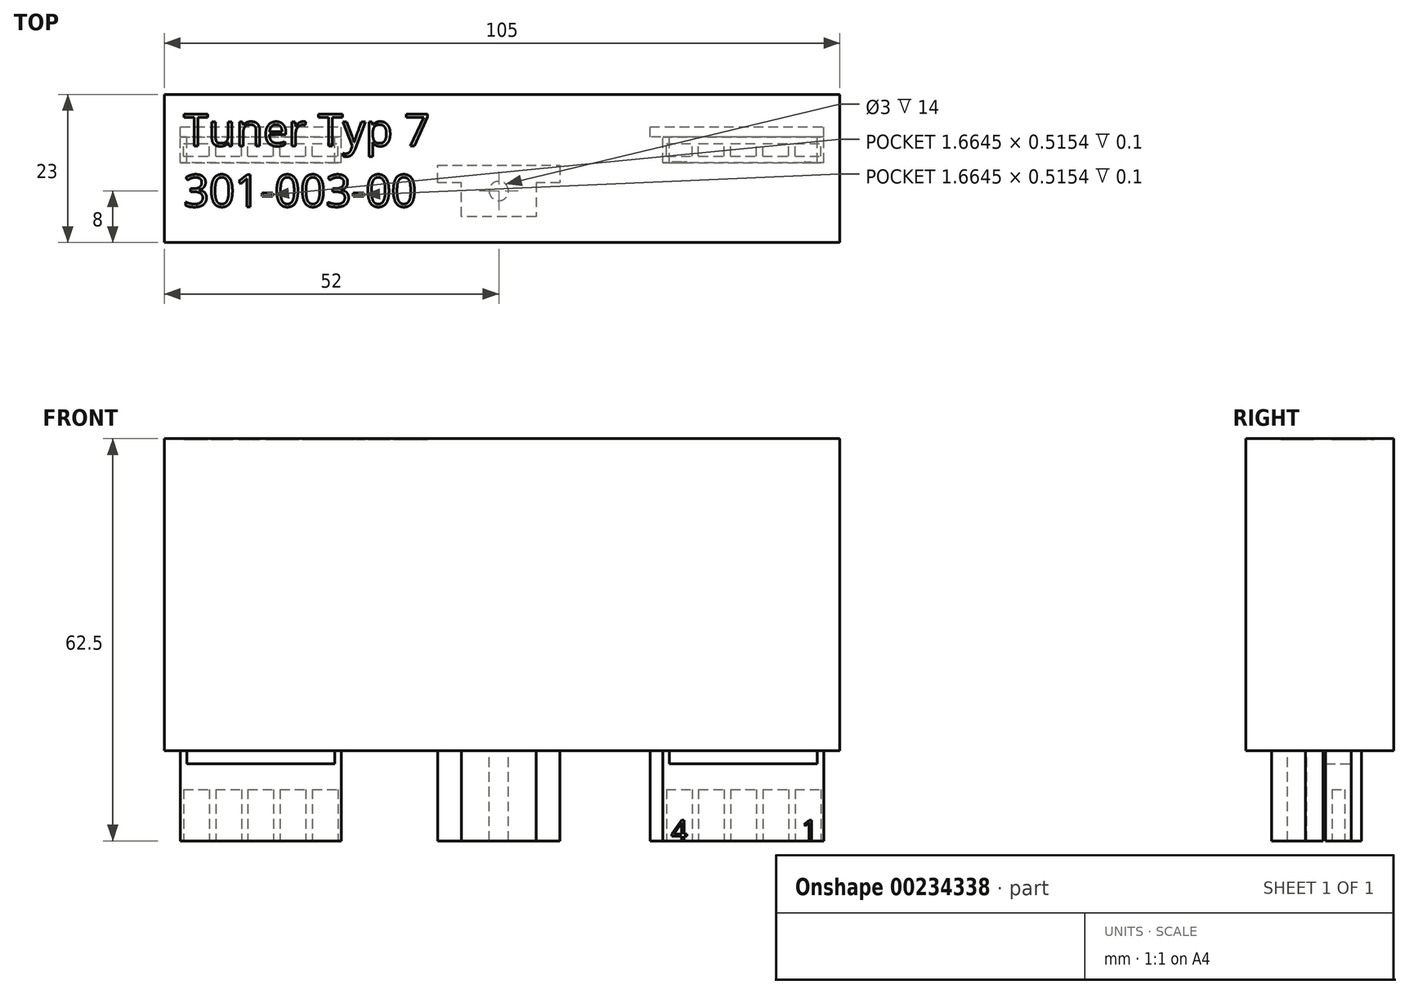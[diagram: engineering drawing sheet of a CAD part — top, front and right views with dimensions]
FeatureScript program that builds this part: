
annotation { "Feature Type Name" : "Feature", "Feature Type Description" : "" }
export const myFeature = defineFeature(function(context is Context, id is Id, definition is map)
    precondition{}
    {
        {
            var Q0;
            Q0=qCreatedBy(makeId("Front.planeOp"),FACE);
            var sketch = newSketch(context, id + "F0", { "sketchPlane" : qUnion([Q0])});
            skLineSegment(sketch, "E0.top", {"start": v(52.5, 24.25) * mm, "end": v(-52.5, 24.25) * mm});
            skLineSegment(sketch, "E0.left", {"start": v(52.5, -24.25) * mm, "end": v(52.5, 24.25) * mm});
            skLineSegment(sketch, "E0.right", {"start": v(-52.5, -24.25) * mm, "end": v(-52.5, 24.25) * mm});
            skPoint(sketch, "E0.middle", {"position": v(0, 0) * mm});
            skLineSegment(sketch, "E1.bottom", {"start": v(-50, -24.25) * mm, "end": v(-25, -24.25) * mm});
            skLineSegment(sketch, "E1.top", {"start": v(-50, -38.25) * mm, "end": v(-25, -38.25) * mm});
            skLineSegment(sketch, "E1.left", {"start": v(-50, -24.25) * mm, "end": v(-50, -38.25) * mm});
            skLineSegment(sketch, "E1.right", {"start": v(-25, -24.25) * mm, "end": v(-25, -38.25) * mm});
            skLineSegment(sketch, "E2.bottom", {"start": v(50, -24.25) * mm, "end": v(23, -24.25) * mm});
            skLineSegment(sketch, "E2.top", {"start": v(50, -38.25) * mm, "end": v(23, -38.25) * mm});
            skLineSegment(sketch, "E2.left", {"start": v(50, -24.25) * mm, "end": v(50, -38.25) * mm});
            skLineSegment(sketch, "E2.right", {"start": v(23, -24.25) * mm, "end": v(23, -38.25) * mm});
            skLineSegment(sketch, "E3", {"start": v(-52.5, -24.25) * mm, "end": v(-50, -24.25) * mm});
            skLineSegment(sketch, "E4", {"start": v(50, -24.25) * mm, "end": v(52.5, -24.25) * mm});
            skLineSegment(sketch, "E5.bottom", {"start": v(-10, -24.25) * mm, "end": v(9, -24.25) * mm});
            skLineSegment(sketch, "E6", {"start": v(-25, -24.25) * mm, "end": v(-10, -24.25) * mm});
            skLineSegment(sketch, "E7", {"start": v(9, -24.25) * mm, "end": v(23, -24.25) * mm});
            skLineSegment(sketch, "E8", {"start": v(-10, -24.25) * mm, "end": v(-10, -38.25) * mm, "construction": true});
            skLineSegment(sketch, "E9", {"start": v(9, -24.25) * mm, "end": v(9, -38.25) * mm, "construction": true});
            skSolve(sketch);
        }
        {
            var Q0;
            Q0=makeQuery(id+"F0.imprint","IMPRINT",FACE,{"disambiguationData":[TD([[makeQuery(id+"F0.imprint","IMPRINT",EDGE,{"derivedFrom":sQuery(id+"F0.wireOp",EDGE,"E0.top")}),1.0]])]});
            var Q1;
            Q1=makeQuery(id+"F0.imprint","IMPRINT",FACE,{"disambiguationData":[TD([[makeQuery(id+"F0.imprint","IMPRINT",EDGE,{"derivedFrom":sQuery(id+"F0.wireOp",EDGE,"E1.bottom")}),-1.0]])]});
            var Q2;
            Q2=makeQuery(id+"F0.imprint","IMPRINT",FACE,{"disambiguationData":[TD([[makeQuery(id+"F0.imprint","IMPRINT",EDGE,{"derivedFrom":sQuery(id+"F0.wireOp",EDGE,"E5.bottom")}),-1.0]])]});
            var Q3;
            Q3=makeQuery(id+"F0.imprint","IMPRINT",FACE,{"disambiguationData":[TD([[makeQuery(id+"F0.imprint","IMPRINT",EDGE,{"derivedFrom":sQuery(id+"F0.wireOp",EDGE,"E2.bottom")}),1.0]])]});
            extrude(context, id + "F1", {"entities" : qUnion([Q0, Q1, Q2, Q3]), "depth" : 1.6 * mm});
        }
        {
            var Q0;
            Q0=makeQuery(id+"F0.imprint","IMPRINT",FACE,{"disambiguationData":[TD([[makeQuery(id+"F0.imprint","IMPRINT",EDGE,{"derivedFrom":sQuery(id+"F0.wireOp",EDGE,"E0.top")}),1.0]])]});
            extrude(context, id + "F2", {"entities" : qUnion([Q0]), "operationType" : NewBodyOperationType.ADD, "oppositeDirection" : true, "depth" : 5 * mm});
        }
        {
            var Q0;
            Q0=makeQuery(id+"F0.imprint","IMPRINT",FACE,{"disambiguationData":[TD([[makeQuery(id+"F0.imprint","IMPRINT",EDGE,{"derivedFrom":sQuery(id+"F0.wireOp",EDGE,"E0.top")}),1.0]])]});
            extrude(context, id + "F3", {"entities" : qUnion([Q0]), "operationType" : NewBodyOperationType.ADD, "depth" : 18 * mm});
        }
        {
            var Q0;
            {var subQ0=sQuery(id+"F0.wireOp",EDGE,"E7");var subQ1=sQuery(id+"F0.wireOp",EDGE,"E6");var subQ2=sQuery(id+"F0.wireOp",EDGE,"E5.bottom");var subQ3=sQuery(id+"F0.wireOp",EDGE,"E4");var subQ4=sQuery(id+"F0.wireOp",EDGE,"E3");var subQ5=sQuery(id+"F0.wireOp",EDGE,"E2.bottom");var subQ6=sQuery(id+"F0.wireOp",EDGE,"E1.bottom");Q0=makeQuery(id+"F3.boolean.opBoolean","MERGE",FACE,{"derivedFrom":[makeQuery(id+"F2.boolean.opBoolean","MERGE",FACE,{"derivedFrom":[makeQuery(id+"F1.opExtrude","SWEPT_FACE",FACE,{"disambiguationData":[OSD([subQ4])]}),makeQuery(id+"F1.opExtrude","SWEPT_FACE",FACE,{"disambiguationData":[OSD([subQ3])]}),makeQuery(id+"F1.opExtrude","SWEPT_FACE",FACE,{"disambiguationData":[OSD([subQ2,subQ1,subQ0])]}),makeQuery(id+"F2.opExtrude","SWEPT_FACE",FACE,{"disambiguationData":[OSD([subQ6,subQ5,subQ4,subQ3,subQ2,subQ1,subQ0])]})]}),makeQuery(id+"F3.opExtrude","SWEPT_FACE",FACE,{"disambiguationData":[OSD([subQ6,subQ5,subQ4,subQ3,subQ2,subQ1,subQ0])]})]});}
            var sketch = newSketch(context, id + "F4", { "sketchPlane" : qUnion([Q0])});
            skLineSegment(sketch, "E10", {"start": v(-10, 6) * mm, "end": v(9, 6) * mm});
            skLineSegment(sketch, "E11", {"start": v(9, 6) * mm, "end": v(9, 8.7) * mm});
            skLineSegment(sketch, "E12", {"start": v(9, 8.7) * mm, "end": v(5.3, 8.7) * mm});
            skLineSegment(sketch, "E13", {"start": v(5.3, 8.7) * mm, "end": v(5.3, 14) * mm});
            skLineSegment(sketch, "E14", {"start": v(5.3, 14) * mm, "end": v(-6.3, 14) * mm});
            skLineSegment(sketch, "E15", {"start": v(-6.3, 14) * mm, "end": v(-6.3, 8.7) * mm});
            skLineSegment(sketch, "E16", {"start": v(-6.3, 8.7) * mm, "end": v(-10, 8.7) * mm});
            skLineSegment(sketch, "E17", {"start": v(-10, 8.7) * mm, "end": v(-10, 6) * mm});
            skCircle(sketch, "E18", {"center": v(-0.5, 10) * mm, "radius": 1.5 * mm});
            skLineSegment(sketch, "E19", {"start": v(-0.5, 14) * mm, "end": v(-0.5, 6) * mm, "construction": true});
            skSolve(sketch);
        }
        {
            var Q0;
            Q0=makeQuery(id+"F4.imprint","IMPRINT",FACE,{"disambiguationData":[TD([[makeQuery(id+"F4.imprint","IMPRINT",EDGE,{"derivedFrom":sQuery(id+"F4.wireOp",EDGE,"E10")}),1.0]])]});
            extrude(context, id + "F5", {"entities" : qUnion([Q0]), "operationType" : NewBodyOperationType.ADD, "depth" : 14 * mm});
        }
        {
            var Q0;
            {var subQ0=sQuery(id+"F0.wireOp",EDGE,"E3");var subQ1=sQuery(id+"F0.wireOp",EDGE,"E1.right");var subQ2=sQuery(id+"F0.wireOp",EDGE,"E1.left");var subQ3=sQuery(id+"F0.wireOp",EDGE,"E7");var subQ4=sQuery(id+"F0.wireOp",EDGE,"E6");var subQ5=sQuery(id+"F0.wireOp",EDGE,"E5.bottom");var subQ6=sQuery(id+"F0.wireOp",EDGE,"E4");var subQ9=sQuery(id+"F0.wireOp",EDGE,"E1.top");Q0=makeQuery(id+"F3.boolean.opBoolean","SPLIT",FACE,{"disambiguationData":[TD([makeQuery(id+"F1.opExtrude","SWEPT_FACE",FACE,{"disambiguationData":[OSD([subQ9])]})])],"derivedFrom":makeQuery(id+"F1.opExtrude","CAP_FACE",FACE,{"disambiguationData":[OSD([sQuery(id+"F0.wireOp",EDGE,"E0.top"),sQuery(id+"F0.wireOp",EDGE,"E0.left"),sQuery(id+"F0.wireOp",EDGE,"E0.right"),subQ9,subQ2,subQ1,sQuery(id+"F0.wireOp",EDGE,"E2.top"),sQuery(id+"F0.wireOp",EDGE,"E2.left"),sQuery(id+"F0.wireOp",EDGE,"E2.right"),subQ0,subQ6,subQ5,subQ4,subQ3])],"isStart":false})});}
            var sketch = newSketch(context, id + "F6", { "sketchPlane" : qUnion([Q0])});
            skLineSegment(sketch, "E20", {"start": v(-50, -24.25) * mm, "end": v(-50, -38.25) * mm});
            skLineSegment(sketch, "E21", {"start": v(-50, -38.25) * mm, "end": v(-25, -38.25) * mm});
            skLineSegment(sketch, "E22", {"start": v(-25, -38.25) * mm, "end": v(-25, -24.25) * mm});
            skLineSegment(sketch, "E23", {"start": v(-25, -24.25) * mm, "end": v(-26, -24.25) * mm});
            skLineSegment(sketch, "E24", {"start": v(-26, -24.25) * mm, "end": v(-26, -26.25) * mm});
            skLineSegment(sketch, "E25", {"start": v(-26, -26.25) * mm, "end": v(-49, -26.25) * mm});
            skLineSegment(sketch, "E26", {"start": v(-49, -26.25) * mm, "end": v(-49, -24.25) * mm});
            skLineSegment(sketch, "E27", {"start": v(-49, -24.25) * mm, "end": v(-50, -24.25) * mm});
            skSolve(sketch);
        }
        {
            var Q0;
            Q0=makeQuery(id+"F6.imprint","IMPRINT",FACE,{"disambiguationData":[TD([[makeQuery(id+"F6.imprint","IMPRINT",EDGE,{"derivedFrom":sQuery(id+"F6.wireOp",EDGE,"E20")}),1.0]])]});
            extrude(context, id + "F7", {"entities" : qUnion([Q0]), "depth" : 4 * mm});
        }
        {
            var Q0;
            Q0=makeQuery(id+"F7.opExtrude","SWEPT_BODY",BODY,{"disambiguationData":[OSD([sQuery(id+"F6.wireOp",EDGE,"E20"),sQuery(id+"F6.wireOp",EDGE,"E21"),sQuery(id+"F6.wireOp",EDGE,"E22"),sQuery(id+"F6.wireOp",EDGE,"E23"),sQuery(id+"F6.wireOp",EDGE,"E24"),sQuery(id+"F6.wireOp",EDGE,"E25"),sQuery(id+"F6.wireOp",EDGE,"E26"),sQuery(id+"F6.wireOp",EDGE,"E27")])]});
            transform(context, id + "F8", {"entities" : qUnion([Q0]), "transformType" : TransformType.TRANSLATION_3D, "dx" : 75 * mm, "dy" : 0 * mm, "dz" : 0 * mm, "makeCopy" : true});
        }
        {
            var Q0;
            {var subQ0=sQuery(id+"F0.wireOp",EDGE,"E0.top");Q0=makeQuery(id+"F3.boolean.opBoolean","MERGE",FACE,{"derivedFrom":[makeQuery(id+"F2.boolean.opBoolean","MERGE",FACE,{"derivedFrom":[makeQuery(id+"F1.opExtrude","SWEPT_FACE",FACE,{"disambiguationData":[OSD([subQ0])]}),makeQuery(id+"F2.opExtrude","SWEPT_FACE",FACE,{"disambiguationData":[OSD([subQ0])]})]}),makeQuery(id+"F3.opExtrude","SWEPT_FACE",FACE,{"disambiguationData":[OSD([subQ0])]})]});}
            var sketch = newSketch(context, id + "F9", { "sketchPlane" : qUnion([Q0])});
            skText(sketch, "E28", { "text": "Tuner Typ 7\n301-003-00", "fontName": "OpenSans-Regular.ttf"});
            const initialGuessF9  = {"E28": [-0.0495, -0.003, 1, 0, 0.005]};
            skSetInitialGuess(sketch, initialGuessF9);
            skSolve(sketch);
        }
        {
            var Q0;
            Q0 = qSketchRegion(id + "F9", true);
            extrude(context, id + "F10", {"entities" : qUnion([Q0]), "operationType" : NewBodyOperationType.REMOVE, "oppositeDirection" : true, "depth" : .1 * mm});
        }
        {
            var Q0;
            Q0=makeQuery(id+"F7.opExtrude","SWEPT_FACE",FACE,{"disambiguationData":[OSD([sQuery(id+"F6.wireOp",EDGE,"E21")])]});
            var sketch = newSketch(context, id + "F11", { "sketchPlane" : qUnion([Q0])});
            skLineSegment(sketch, "E29.bottom", {"start": v(-50, 5.6) * mm, "end": v(-25, 5.6) * mm, "construction": true});
            skLineSegment(sketch, "E29.top", {"start": v(-50, 1.6) * mm, "end": v(-25, 1.6) * mm, "construction": true});
            skLineSegment(sketch, "E29.left", {"start": v(-50, 5.6) * mm, "end": v(-50, 1.6) * mm, "construction": true});
            skLineSegment(sketch, "E29.right", {"start": v(-25, 5.6) * mm, "end": v(-25, 1.6) * mm, "construction": true});
            skLineSegment(sketch, "E30.bottom", {"start": v(-49.5, 4.6) * mm, "end": v(-45.5, 4.6) * mm});
            skLineSegment(sketch, "E30.top", {"start": v(-49.5, 2.6) * mm, "end": v(-45.5, 2.6) * mm});
            skLineSegment(sketch, "E30.left", {"start": v(-49.5, 4.6) * mm, "end": v(-49.5, 2.6) * mm});
            skLineSegment(sketch, "E30.right", {"start": v(-45.5, 4.6) * mm, "end": v(-45.5, 2.6) * mm});
            skPoint(sketch, "E31", {"position": v(-50, 3.6) * mm});
            skPoint(sketch, "E32", {"position": v(-49.5, 3.6) * mm});
            skLineSegment(sketch, "E33.1.0.0", {"start": v(-44.5, 2.6) * mm, "end": v(-40.5, 2.6) * mm});
            skLineSegment(sketch, "E33.1.0.1", {"start": v(-44.5, 4.6) * mm, "end": v(-44.5, 2.6) * mm});
            skLineSegment(sketch, "E33.1.0.2", {"start": v(-44.5, 4.6) * mm, "end": v(-40.5, 4.6) * mm});
            skLineSegment(sketch, "E33.1.0.3", {"start": v(-40.5, 4.6) * mm, "end": v(-40.5, 2.6) * mm});
            skLineSegment(sketch, "E33.2.0.0", {"start": v(-39.5, 2.6) * mm, "end": v(-35.5, 2.6) * mm});
            skLineSegment(sketch, "E33.2.0.1", {"start": v(-39.5, 4.6) * mm, "end": v(-39.5, 2.6) * mm});
            skLineSegment(sketch, "E33.2.0.2", {"start": v(-39.5, 4.6) * mm, "end": v(-35.5, 4.6) * mm});
            skLineSegment(sketch, "E33.2.0.3", {"start": v(-35.5, 4.6) * mm, "end": v(-35.5, 2.6) * mm});
            skLineSegment(sketch, "E33.3.0.0", {"start": v(-34.5, 2.6) * mm, "end": v(-30.5, 2.6) * mm});
            skLineSegment(sketch, "E33.3.0.1", {"start": v(-34.5, 4.6) * mm, "end": v(-34.5, 2.6) * mm});
            skLineSegment(sketch, "E33.3.0.2", {"start": v(-34.5, 4.6) * mm, "end": v(-30.5, 4.6) * mm});
            skLineSegment(sketch, "E33.3.0.3", {"start": v(-30.5, 4.6) * mm, "end": v(-30.5, 2.6) * mm});
            skLineSegment(sketch, "E33.4.0.0", {"start": v(-29.5, 2.6) * mm, "end": v(-25.5, 2.6) * mm});
            skLineSegment(sketch, "E33.4.0.1", {"start": v(-29.5, 4.6) * mm, "end": v(-29.5, 2.6) * mm});
            skLineSegment(sketch, "E33.4.0.2", {"start": v(-29.5, 4.6) * mm, "end": v(-25.5, 4.6) * mm});
            skLineSegment(sketch, "E33.4.0.3", {"start": v(-25.5, 4.6) * mm, "end": v(-25.5, 2.6) * mm});
            skLineSegment(sketch, "E33.direction1", {"start": v(-49.5, 2.6) * mm, "end": v(-44.5, 2.6) * mm, "construction": true});
            skSolve(sketch);
        }
        {
            var Q0;
            Q0=makeQuery(id+"F11.imprint","IMPRINT",FACE,{"disambiguationData":[TD([[makeQuery(id+"F11.imprint","IMPRINT",EDGE,{"derivedFrom":sQuery(id+"F11.wireOp",EDGE,"E30.bottom")}),-1.0]])]});
            var Q1;
            Q1=makeQuery(id+"F11.imprint","IMPRINT",FACE,{"disambiguationData":[TD([[makeQuery(id+"F11.imprint","IMPRINT",EDGE,{"derivedFrom":sQuery(id+"F11.wireOp",EDGE,"E33.1.0.0")}),1.0]])]});
            var Q2;
            Q2=makeQuery(id+"F11.imprint","IMPRINT",FACE,{"disambiguationData":[TD([[makeQuery(id+"F11.imprint","IMPRINT",EDGE,{"derivedFrom":sQuery(id+"F11.wireOp",EDGE,"E33.2.0.0")}),1.0]])]});
            var Q3;
            Q3=makeQuery(id+"F11.imprint","IMPRINT",FACE,{"disambiguationData":[TD([[makeQuery(id+"F11.imprint","IMPRINT",EDGE,{"derivedFrom":sQuery(id+"F11.wireOp",EDGE,"E33.3.0.0")}),1.0]])]});
            var Q4;
            Q4=makeQuery(id+"F11.imprint","IMPRINT",FACE,{"disambiguationData":[TD([[makeQuery(id+"F11.imprint","IMPRINT",EDGE,{"derivedFrom":sQuery(id+"F11.wireOp",EDGE,"E33.4.0.0")}),1.0]])]});
            extrude(context, id + "F12", {"entities" : qUnion([Q0, Q1, Q2, Q3, Q4]), "operationType" : NewBodyOperationType.REMOVE, "oppositeDirection" : true, "depth" : 8 * mm});
        }
        {
            var Q0;
            Q0=makeQuery(id+"F8.opPattern","COPY",FACE,{"derivedFrom":makeQuery(id+"F7.opExtrude","SWEPT_FACE",FACE,{"disambiguationData":[OSD([sQuery(id+"F6.wireOp",EDGE,"E21")])]}),"instanceName":"1"});
            var sketch = newSketch(context, id + "F13", { "sketchPlane" : qUnion([Q0])});
            skLineSegment(sketch, "E34.bottom", {"start": v(25.03, 5.55) * mm, "end": v(50.03, 5.55) * mm, "construction": true});
            skLineSegment(sketch, "E34.top", {"start": v(25.03, 1.64) * mm, "end": v(50.03, 1.64) * mm, "construction": true});
            skLineSegment(sketch, "E34.left", {"start": v(25.03, 5.55) * mm, "end": v(25.03, 1.64) * mm, "construction": true});
            skLineSegment(sketch, "E34.right", {"start": v(50.03, 5.55) * mm, "end": v(50.03, 1.64) * mm, "construction": true});
            skLineSegment(sketch, "E35.bottom", {"start": v(25.53, 4.6) * mm, "end": v(29.53, 4.6) * mm});
            skLineSegment(sketch, "E35.top", {"start": v(25.53, 2.6) * mm, "end": v(29.53, 2.6) * mm});
            skLineSegment(sketch, "E35.left", {"start": v(25.53, 4.6) * mm, "end": v(25.53, 2.6) * mm});
            skLineSegment(sketch, "E35.right", {"start": v(29.53, 4.6) * mm, "end": v(29.53, 2.6) * mm});
            skPoint(sketch, "E36", {"position": v(25, 3.6) * mm});
            skPoint(sketch, "E37", {"position": v(25.53, 3.6) * mm});
            skLineSegment(sketch, "E38.1.0.0", {"start": v(30.53, 2.6) * mm, "end": v(34.53, 2.6) * mm});
            skLineSegment(sketch, "E38.1.0.1", {"start": v(30.53, 4.6) * mm, "end": v(30.53, 2.6) * mm});
            skLineSegment(sketch, "E38.1.0.2", {"start": v(30.53, 4.6) * mm, "end": v(34.53, 4.6) * mm});
            skLineSegment(sketch, "E38.1.0.3", {"start": v(34.53, 4.6) * mm, "end": v(34.53, 2.6) * mm});
            skLineSegment(sketch, "E38.2.0.0", {"start": v(35.53, 2.6) * mm, "end": v(39.53, 2.6) * mm});
            skLineSegment(sketch, "E38.2.0.1", {"start": v(35.53, 4.6) * mm, "end": v(35.53, 2.6) * mm});
            skLineSegment(sketch, "E38.2.0.2", {"start": v(35.53, 4.6) * mm, "end": v(39.53, 4.6) * mm});
            skLineSegment(sketch, "E38.2.0.3", {"start": v(39.53, 4.6) * mm, "end": v(39.53, 2.6) * mm});
            skLineSegment(sketch, "E38.3.0.0", {"start": v(40.53, 2.6) * mm, "end": v(44.53, 2.6) * mm});
            skLineSegment(sketch, "E38.3.0.1", {"start": v(40.53, 4.6) * mm, "end": v(40.53, 2.6) * mm});
            skLineSegment(sketch, "E38.3.0.2", {"start": v(40.53, 4.6) * mm, "end": v(44.53, 4.6) * mm});
            skLineSegment(sketch, "E38.3.0.3", {"start": v(44.53, 4.6) * mm, "end": v(44.53, 2.6) * mm});
            skLineSegment(sketch, "E38.4.0.0", {"start": v(45.53, 2.6) * mm, "end": v(49.53, 2.6) * mm});
            skLineSegment(sketch, "E38.4.0.1", {"start": v(45.53, 4.6) * mm, "end": v(45.53, 2.6) * mm});
            skLineSegment(sketch, "E38.4.0.2", {"start": v(45.53, 4.6) * mm, "end": v(49.53, 4.6) * mm});
            skLineSegment(sketch, "E38.4.0.3", {"start": v(49.53, 4.6) * mm, "end": v(49.53, 2.6) * mm});
            skLineSegment(sketch, "E38.direction1", {"start": v(25.53, 2.6) * mm, "end": v(30.53, 2.6) * mm, "construction": true});
            skSolve(sketch);
        }
        {
            var Q0;
            Q0=makeQuery(id+"F13.imprint","IMPRINT",FACE,{"disambiguationData":[TD([[makeQuery(id+"F13.imprint","IMPRINT",EDGE,{"derivedFrom":sQuery(id+"F13.wireOp",EDGE,"E38.1.0.0")}),1.0]])]});
            var Q1;
            Q1=makeQuery(id+"F13.imprint","IMPRINT",FACE,{"disambiguationData":[TD([[makeQuery(id+"F13.imprint","IMPRINT",EDGE,{"derivedFrom":sQuery(id+"F13.wireOp",EDGE,"E38.2.0.0")}),1.0]])]});
            var Q2;
            Q2=makeQuery(id+"F13.imprint","IMPRINT",FACE,{"disambiguationData":[TD([[makeQuery(id+"F13.imprint","IMPRINT",EDGE,{"derivedFrom":sQuery(id+"F13.wireOp",EDGE,"E38.3.0.0")}),1.0]])]});
            var Q3;
            Q3=makeQuery(id+"F13.imprint","IMPRINT",FACE,{"disambiguationData":[TD([[makeQuery(id+"F13.imprint","IMPRINT",EDGE,{"derivedFrom":sQuery(id+"F13.wireOp",EDGE,"E38.4.0.0")}),1.0]])]});
            var Q4;
            Q4=makeQuery(id+"F13.imprint","IMPRINT",FACE,{"disambiguationData":[TD([[makeQuery(id+"F13.imprint","IMPRINT",EDGE,{"derivedFrom":sQuery(id+"F13.wireOp",EDGE,"E35.bottom")}),-1.0]])]});
            extrude(context, id + "F14", {"entities" : qUnion([Q0, Q1, Q2, Q3, Q4]), "operationType" : NewBodyOperationType.REMOVE, "oppositeDirection" : true, "depth" : 8 * mm});
        }
        {
            var Q0;
            Q0=makeQuery(id+"F8.opPattern","COPY",FACE,{"derivedFrom":makeQuery(id+"F7.opExtrude","CAP_FACE",FACE,{"disambiguationData":[OSD([sQuery(id+"F6.wireOp",EDGE,"E20"),sQuery(id+"F6.wireOp",EDGE,"E21"),sQuery(id+"F6.wireOp",EDGE,"E22"),sQuery(id+"F6.wireOp",EDGE,"E23"),sQuery(id+"F6.wireOp",EDGE,"E24"),sQuery(id+"F6.wireOp",EDGE,"E25"),sQuery(id+"F6.wireOp",EDGE,"E26"),sQuery(id+"F6.wireOp",EDGE,"E27")])],"isStart":false}),"instanceName":"1"});
            var sketch = newSketch(context, id + "F15", { "sketchPlane" : qUnion([Q0])});
            skText(sketch, "E39", { "text": "1", "fontName": "OpenSans-Regular.ttf"});
            skText(sketch, "E40", { "text": "4", "fontName": "OpenSans-Regular.ttf"});
            const initialGuessF15  = {"E39": [0.04652, -0.03825, 1, 0, 0.00324], "E40": [0.02626, -0.03825, 1, 0, 0.00324]};
            skSetInitialGuess(sketch, initialGuessF15);
            skSolve(sketch);
        }
        {
            var Q0;
            Q0 = qSketchRegion(id + "F15", true);
            extrude(context, id + "F16", {"entities" : qUnion([Q0]), "operationType" : NewBodyOperationType.REMOVE, "oppositeDirection" : true, "depth" : .1 * mm});
        }
    });
